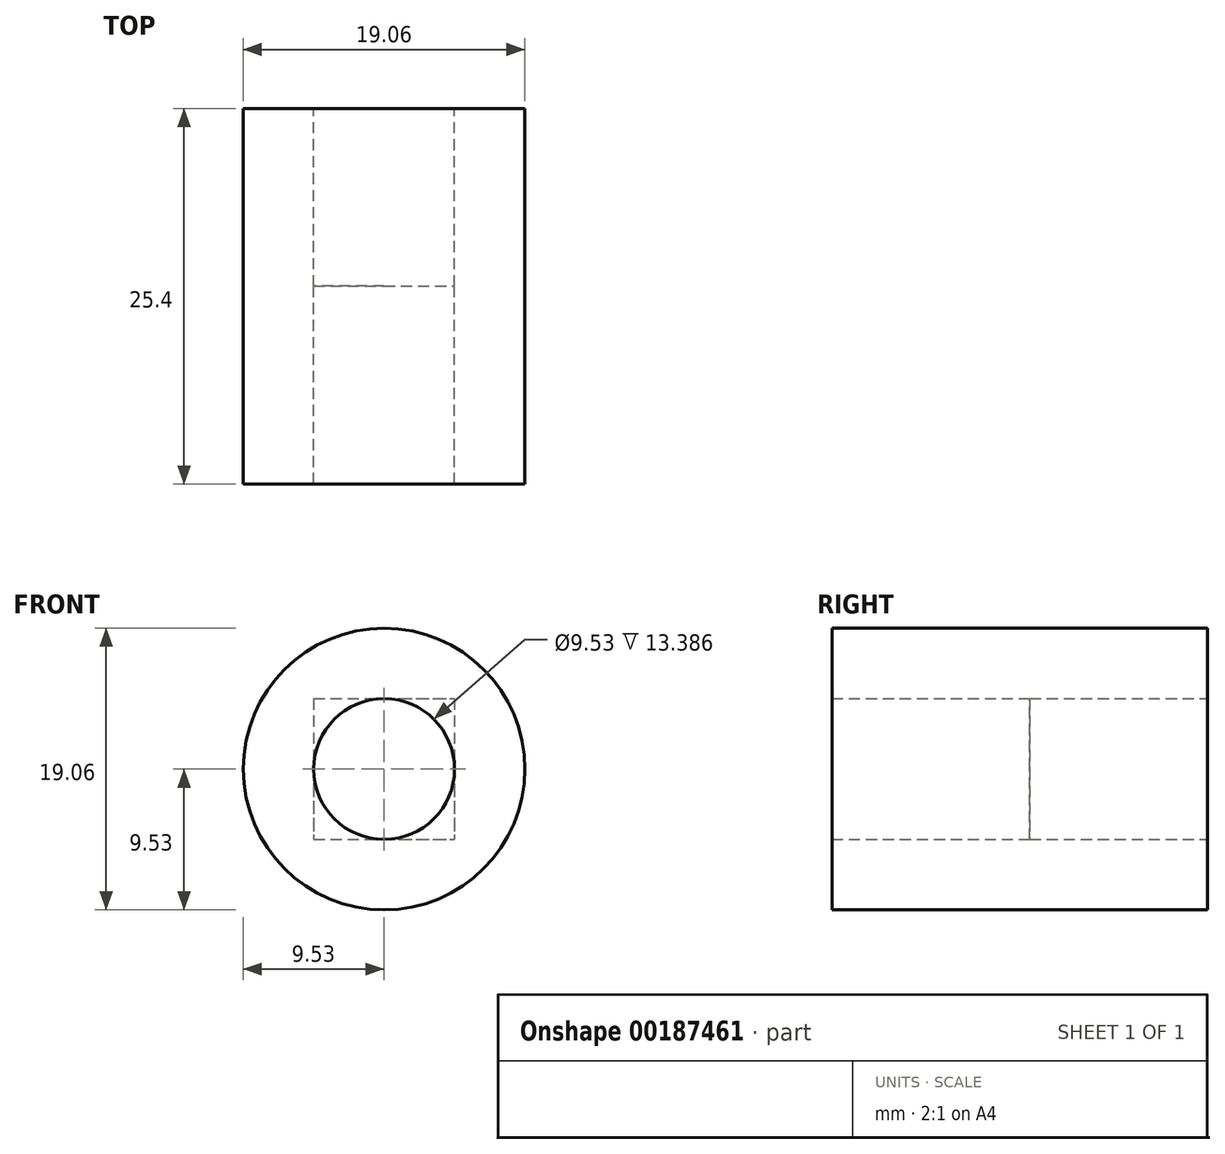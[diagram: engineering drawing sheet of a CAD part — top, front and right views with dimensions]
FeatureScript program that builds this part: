
annotation { "Feature Type Name" : "Feature", "Feature Type Description" : "" }
export const myFeature = defineFeature(function(context is Context, id is Id, definition is map)
    precondition{}
    {
        {
            var Q0;
            Q0=qCreatedBy(makeId("Front.planeOp"),FACE);
            var sketch = newSketch(context, id + "F0", { "sketchPlane" : qUnion([Q0])});
            skCircle(sketch, "E0", {"center": v(0, 0) * mm, "radius": 9.53 * mm});
            skLineSegment(sketch, "E1.bottom", {"start": v(-4.76, 4.76) * mm, "end": v(4.76, 4.76) * mm});
            skLineSegment(sketch, "E1.top", {"start": v(-4.76, -4.76) * mm, "end": v(4.76, -4.76) * mm});
            skLineSegment(sketch, "E1.left", {"start": v(-4.76, 4.76) * mm, "end": v(-4.76, -4.76) * mm});
            skLineSegment(sketch, "E1.right", {"start": v(4.76, 4.76) * mm, "end": v(4.76, -4.76) * mm});
            skCircle(sketch, "E2", {"center": v(0, 0) * mm, "radius": 4.76 * mm});
            skSolve(sketch);
        }
        {
            var Q0;
            Q0=makeQuery(id+"F0.imprint","IMPRINT",FACE,{"disambiguationData":[TD([[makeQuery(id+"F0.imprint","IMPRINT",EDGE,{"derivedFrom":sQuery(id+"F0.wireOp",EDGE,"E0")}),1.0]])]});
            var Q1;
            {var subQ0=sQuery(id+"F0.wireOp",EDGE,"E1.right");var subQ1=sQuery(id+"F0.wireOp",EDGE,"E1.bottom");var subQ2=makeQuery(id+"F0.imprint","INTERSECT",VERTEX,{"derivedFrom":[subQ1,subQ0]});Q1=makeQuery(id+"F0.imprint","IMPRINT",FACE,{"disambiguationData":[TD([[makeQuery(id+"F0.imprint","IMPRINT",EDGE,{"disambiguationData":[TD([[subQ2,1.0]])],"derivedFrom":subQ1}),-1.0]])]});}
            var Q2;
            {var subQ0=sQuery(id+"F0.wireOp",EDGE,"E2");var subQ1=makeQuery(id+"F0.imprint","INTERSECT",VERTEX,{"derivedFrom":[sQuery(id+"F0.wireOp",EDGE,"E1.bottom"),subQ0]});Q2=makeQuery(id+"F0.imprint","IMPRINT",FACE,{"disambiguationData":[TD([[makeQuery(id+"F0.imprint","IMPRINT",EDGE,{"disambiguationData":[TD([[subQ1,1.0]])],"derivedFrom":subQ0}),1.0]])]});}
            var Q3;
            {var subQ0=sQuery(id+"F0.wireOp",EDGE,"E1.left");var subQ1=sQuery(id+"F0.wireOp",EDGE,"E1.top");var subQ2=makeQuery(id+"F0.imprint","INTERSECT",VERTEX,{"derivedFrom":[subQ1,subQ0]});Q3=makeQuery(id+"F0.imprint","IMPRINT",FACE,{"disambiguationData":[TD([[makeQuery(id+"F0.imprint","IMPRINT",EDGE,{"disambiguationData":[TD([[subQ2,-1.0]])],"derivedFrom":subQ1}),1.0]])]});}
            var Q4;
            {var subQ0=sQuery(id+"F0.wireOp",EDGE,"E1.right");var subQ1=sQuery(id+"F0.wireOp",EDGE,"E1.top");var subQ2=makeQuery(id+"F0.imprint","INTERSECT",VERTEX,{"derivedFrom":[subQ1,subQ0]});Q4=makeQuery(id+"F0.imprint","IMPRINT",FACE,{"disambiguationData":[TD([[makeQuery(id+"F0.imprint","IMPRINT",EDGE,{"disambiguationData":[TD([[subQ2,1.0]])],"derivedFrom":subQ1}),1.0]])]});}
            var Q5;
            {var subQ0=sQuery(id+"F0.wireOp",EDGE,"E1.left");var subQ1=sQuery(id+"F0.wireOp",EDGE,"E1.bottom");var subQ2=makeQuery(id+"F0.imprint","INTERSECT",VERTEX,{"derivedFrom":[subQ1,subQ0]});Q5=makeQuery(id+"F0.imprint","IMPRINT",FACE,{"disambiguationData":[TD([[makeQuery(id+"F0.imprint","IMPRINT",EDGE,{"disambiguationData":[TD([[subQ2,-1.0]])],"derivedFrom":subQ1}),-1.0]])]});}
            extrude(context, id + "F1", {"entities" : qUnion([Q0, Q1, Q2, Q3, Q4, Q5]), "depth" : 25.4 * mm});
        }
        {
            var Q0;
            {var subQ0=sQuery(id+"F0.wireOp",EDGE,"E2");var subQ1=makeQuery(id+"F0.imprint","INTERSECT",VERTEX,{"derivedFrom":[sQuery(id+"F0.wireOp",EDGE,"E1.bottom"),subQ0]});Q0=makeQuery(id+"F0.imprint","IMPRINT",FACE,{"disambiguationData":[TD([[makeQuery(id+"F0.imprint","IMPRINT",EDGE,{"disambiguationData":[TD([[subQ1,1.0]])],"derivedFrom":subQ0}),1.0]])]});}
            extrude(context, id + "F2", {"entities" : qUnion([Q0]), "operationType" : NewBodyOperationType.REMOVE, "depth" : 25.4 * mm});
        }
        {
            var Q0;
            {var subQ0=sQuery(id+"F0.wireOp",EDGE,"E1.left");var subQ1=sQuery(id+"F0.wireOp",EDGE,"E1.top");var subQ2=makeQuery(id+"F0.imprint","INTERSECT",VERTEX,{"derivedFrom":[subQ1,subQ0]});Q0=makeQuery(id+"F0.imprint","IMPRINT",FACE,{"disambiguationData":[TD([[makeQuery(id+"F0.imprint","IMPRINT",EDGE,{"disambiguationData":[TD([[subQ2,-1.0]])],"derivedFrom":subQ1}),1.0]])]});}
            var Q1;
            {var subQ0=sQuery(id+"F0.wireOp",EDGE,"E1.right");var subQ1=sQuery(id+"F0.wireOp",EDGE,"E1.top");var subQ2=makeQuery(id+"F0.imprint","INTERSECT",VERTEX,{"derivedFrom":[subQ1,subQ0]});Q1=makeQuery(id+"F0.imprint","IMPRINT",FACE,{"disambiguationData":[TD([[makeQuery(id+"F0.imprint","IMPRINT",EDGE,{"disambiguationData":[TD([[subQ2,1.0]])],"derivedFrom":subQ1}),1.0]])]});}
            var Q2;
            {var subQ0=sQuery(id+"F0.wireOp",EDGE,"E1.left");var subQ1=sQuery(id+"F0.wireOp",EDGE,"E1.bottom");var subQ2=makeQuery(id+"F0.imprint","INTERSECT",VERTEX,{"derivedFrom":[subQ1,subQ0]});Q2=makeQuery(id+"F0.imprint","IMPRINT",FACE,{"disambiguationData":[TD([[makeQuery(id+"F0.imprint","IMPRINT",EDGE,{"disambiguationData":[TD([[subQ2,-1.0]])],"derivedFrom":subQ1}),-1.0]])]});}
            var Q3;
            {var subQ0=sQuery(id+"F0.wireOp",EDGE,"E1.right");var subQ1=sQuery(id+"F0.wireOp",EDGE,"E1.bottom");var subQ2=makeQuery(id+"F0.imprint","INTERSECT",VERTEX,{"derivedFrom":[subQ1,subQ0]});Q3=makeQuery(id+"F0.imprint","IMPRINT",FACE,{"disambiguationData":[TD([[makeQuery(id+"F0.imprint","IMPRINT",EDGE,{"disambiguationData":[TD([[subQ2,1.0]])],"derivedFrom":subQ1}),-1.0]])]});}
            extrude(context, id + "F3", {"entities" : qUnion([Q0, Q1, Q2, Q3]), "operationType" : NewBodyOperationType.REMOVE, "depth" : 12 * mm});
        }
    });
